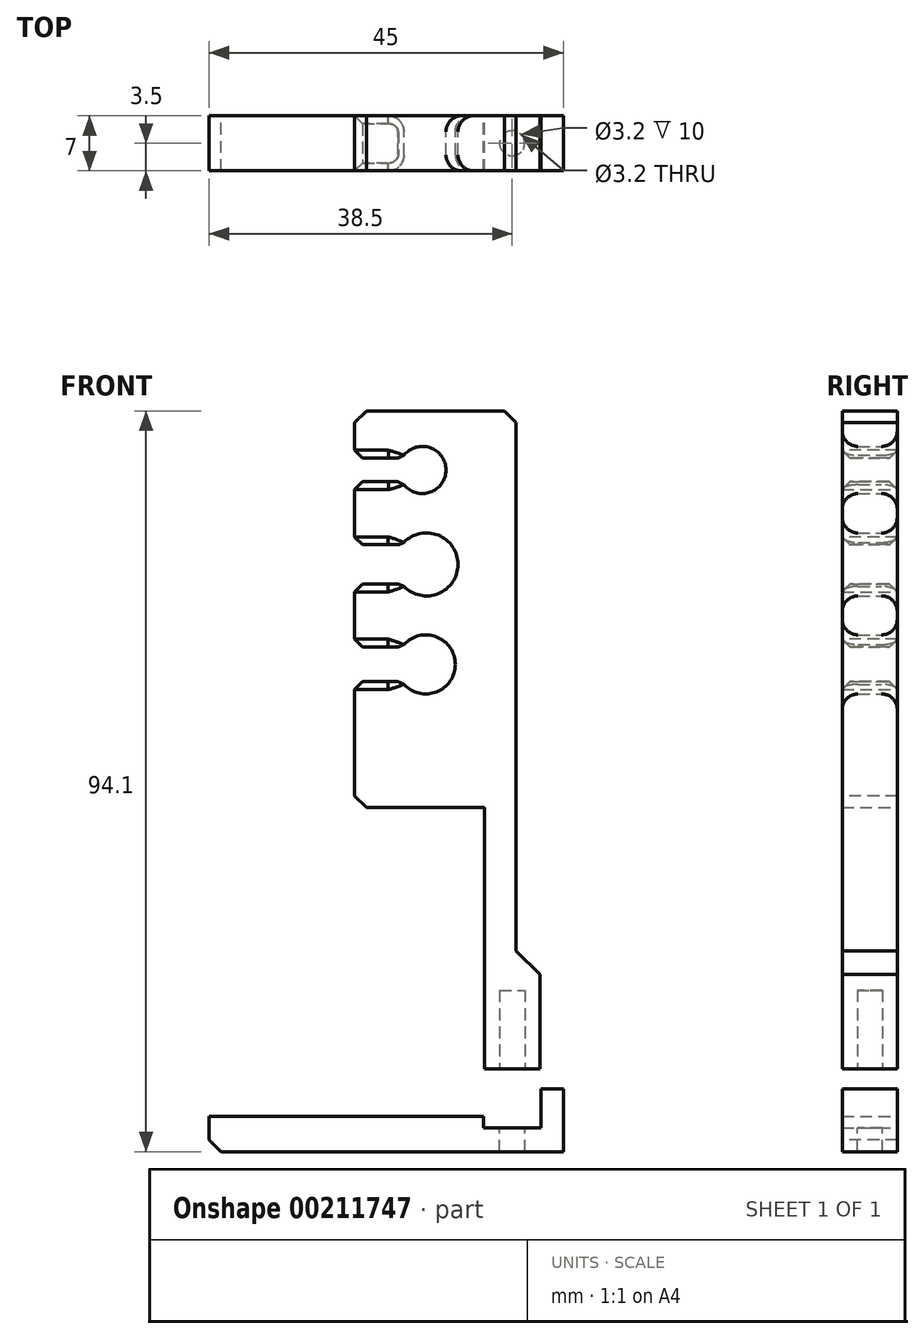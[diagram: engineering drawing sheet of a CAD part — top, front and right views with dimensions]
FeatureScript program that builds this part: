
annotation { "Feature Type Name" : "Feature", "Feature Type Description" : "" }
export const myFeature = defineFeature(function(context is Context, id is Id, definition is map)
    precondition{}
    {
        {
            var Q0;
            Q0=qCreatedBy(makeId("Front.planeOp"),FACE);
            var sketch = newSketch(context, id + "F0", { "sketchPlane" : qUnion([Q0])});
            skLineSegment(sketch, "E0", {"start": v(4, 50.4) * mm, "end": v(-16.51, 50.4) * mm});
            skLineSegment(sketch, "E1", {"start": v(-16.51, 50.4) * mm, "end": v(-16.51, 44.4) * mm});
            skLineSegment(sketch, "E2", {"start": v(-16.51, 44.4) * mm, "end": v(-10.51, 44.4) * mm});
            skLineSegment(sketch, "E3", {"start": v(-16.51, 41.4) * mm, "end": v(-10.51, 41.4) * mm});
            skArc(sketch, "E4", {"start": v(-10.51, 41.4) * mm, "mid": v(-4.91, 42.9) * mm, "end": v(-10.51, 44.4) * mm});
            skLineSegment(sketch, "E5", {"start": v(-16.51, 41.4) * mm, "end": v(-16.51, 33.4) * mm});
            skLineSegment(sketch, "E6", {"start": v(-16.51, 33.4) * mm, "end": v(-10.51, 33.4) * mm});
            skLineSegment(sketch, "E7", {"start": v(-10.5, 28.4) * mm, "end": v(-16.51, 28.4) * mm});
            skLineSegment(sketch, "E8", {"start": v(-16.51, 28.4) * mm, "end": v(-16.51, 20.4) * mm});
            skArc(sketch, "E9", {"start": v(-10.5, 28.4) * mm, "mid": v(-3.39, 30.9) * mm, "end": v(-10.51, 33.4) * mm});
            skLineSegment(sketch, "E10", {"start": v(-16.51, 20.4) * mm, "end": v(-10.51, 20.4) * mm});
            skLineSegment(sketch, "E11", {"start": v(-10.51, 16) * mm, "end": v(-16.51, 16) * mm});
            skArc(sketch, "E12", {"start": v(-10.51, 16) * mm, "mid": v(-3.72, 18.2) * mm, "end": v(-10.51, 20.4) * mm});
            skLineSegment(sketch, "E13.0", {"start": v(3.5, -43.7) * mm, "end": v(-35, -43.7) * mm});
            skPoint(sketch, "E14.end.orphan", {"position": v(-10.51, 18.2) * mm});
            skPoint(sketch, "E15.end.orphan", {"position": v(-10.51, 30.9) * mm});
            skPoint(sketch, "E16.orphan", {"position": v(-20, 0) * mm});
            skLineSegment(sketch, "E17", {"start": v(-35, -39.2) * mm, "end": v(-35, -43.7) * mm});
            skLineSegment(sketch, "E18.trimOffspring", {"start": v(-16.51, 16) * mm, "end": v(-16.51, 0) * mm});
            skPoint(sketch, "E19.start.orphan", {"position": v(0, 0) * mm});
            skLineSegment(sketch, "E20", {"start": v(0, -33.2) * mm, "end": v(0, 0) * mm});
            skLineSegment(sketch, "E21", {"start": v(4, 0.1) * mm, "end": v(4, -21.2) * mm});
            skLineSegment(sketch, "E22", {"start": v(-16.51, 0) * mm, "end": v(0, 0) * mm});
            skLineSegment(sketch, "E23", {"start": v(4, 50.4) * mm, "end": v(4, 0.1) * mm});
            skLineSegment(sketch, "E24", {"start": v(3.5, -43.7) * mm, "end": v(6.5, -43.7) * mm});
            skLineSegment(sketch, "E25", {"start": v(6.5, -43.7) * mm, "end": v(6.5, -40.7) * mm});
            skLineSegment(sketch, "E26", {"start": v(0, -33.2) * mm, "end": v(4, -33.2) * mm});
            skLineSegment(sketch, "E27", {"start": v(4, -33.2) * mm, "end": v(7, -33.2) * mm});
            skPoint(sketch, "E28.end.orphan", {"position": v(3.5, -40.7) * mm});
            skPoint(sketch, "E29.start.orphan", {"position": v(0, -40.7) * mm});
            skLineSegment(sketch, "E30", {"start": v(-35, -39.2) * mm, "end": v(-0.15, -39.2) * mm});
            skLineSegment(sketch, "E31", {"start": v(7, -33.2) * mm, "end": v(7, -21.2) * mm});
            skLineSegment(sketch, "E32", {"start": v(7, -21.2) * mm, "end": v(4, -21.2) * mm});
            skLineSegment(sketch, "E33", {"start": v(6.5, -43.7) * mm, "end": v(10, -43.7) * mm});
            skLineSegment(sketch, "E34", {"start": v(10, -43.7) * mm, "end": v(10, -35.7) * mm});
            skLineSegment(sketch, "E35", {"start": v(10, -35.7) * mm, "end": v(7.15, -35.7) * mm});
            skLineSegment(sketch, "E36", {"start": v(6.5, -40.7) * mm, "end": v(0, -40.7) * mm});
            skLineSegment(sketch, "E37", {"start": v(6.5, -40.7) * mm, "end": v(7.15, -40.7) * mm});
            skLineSegment(sketch, "E38", {"start": v(7.15, -40.7) * mm, "end": v(7.15, -35.7) * mm});
            skLineSegment(sketch, "E39", {"start": v(0, -40.7) * mm, "end": v(-0.15, -40.7) * mm});
            skLineSegment(sketch, "E40", {"start": v(-0.15, -40.7) * mm, "end": v(-0.15, -39.2) * mm});
            skPoint(sketch, "E41.orphan", {"position": v(6.5, -35.7) * mm});
            skPoint(sketch, "E42.orphan", {"position": v(6.5, -39.2) * mm});
            skSolve(sketch);
        }
        {
            var Q0;
            Q0 = qSketchRegion(id + "F0", true);
            extrude(context, id + "F1", {"entities" : qUnion([Q0]), "depth" : 7 * mm});
        }
        {
            var Q0;
            Q0=makeQuery(id+"F1.opExtrude","CAP_EDGE",EDGE,{"disambiguationData":[OSD([sQuery(id+"F0.wireOp",EDGE,"E12")])],"isStart":false});
            var Q1;
            Q1=makeQuery(id+"F1.opExtrude","CAP_EDGE",EDGE,{"disambiguationData":[OSD([sQuery(id+"F0.wireOp",EDGE,"E9")])],"isStart":false});
            var Q2;
            Q2=makeQuery(id+"F1.opExtrude","CAP_EDGE",EDGE,{"disambiguationData":[OSD([sQuery(id+"F0.wireOp",EDGE,"E4")])],"isStart":false});
            var Q3;
            Q3=makeQuery(id+"F1.opExtrude","CAP_EDGE",EDGE,{"disambiguationData":[OSD([sQuery(id+"F0.wireOp",EDGE,"E4")])],"isStart":true});
            var Q4;
            Q4=makeQuery(id+"F1.opExtrude","CAP_EDGE",EDGE,{"disambiguationData":[OSD([sQuery(id+"F0.wireOp",EDGE,"E9")])],"isStart":true});
            var Q5;
            Q5=makeQuery(id+"F1.opExtrude","CAP_EDGE",EDGE,{"disambiguationData":[OSD([sQuery(id+"F0.wireOp",EDGE,"E12")])],"isStart":true});
            fillet(context, id + "F2", {"entities" : qUnion([Q0, Q1, Q2, Q3, Q4, Q5]), "radius" : 2 * mm, "tangentPropagation" : true, "allowEdgeOverflow" : false});
        }
        {
            var Q0;
            Q0=makeQuery(id+"F1.opExtrude","SWEPT_EDGE",EDGE,{"disambiguationData":[OSD([sQuery(id+"F0.wireOp",EDGE,"E11"),sQuery(id+"F0.wireOp",EDGE,"E18.trimOffspring")])]});
            var Q1;
            Q1=makeQuery(id+"F1.opExtrude","SWEPT_EDGE",EDGE,{"disambiguationData":[OSD([sQuery(id+"F0.wireOp",EDGE,"E10"),sQuery(id+"F0.wireOp",EDGE,"E8")])]});
            var Q2;
            Q2=makeQuery(id+"F1.opExtrude","SWEPT_EDGE",EDGE,{"disambiguationData":[OSD([sQuery(id+"F0.wireOp",EDGE,"E7"),sQuery(id+"F0.wireOp",EDGE,"E8")])]});
            var Q3;
            Q3=makeQuery(id+"F1.opExtrude","SWEPT_EDGE",EDGE,{"disambiguationData":[OSD([sQuery(id+"F0.wireOp",EDGE,"E6"),sQuery(id+"F0.wireOp",EDGE,"E5")])]});
            var Q4;
            Q4=makeQuery(id+"F1.opExtrude","SWEPT_EDGE",EDGE,{"disambiguationData":[OSD([sQuery(id+"F0.wireOp",EDGE,"E3"),sQuery(id+"F0.wireOp",EDGE,"E5")])]});
            var Q5;
            Q5=makeQuery(id+"F1.opExtrude","SWEPT_EDGE",EDGE,{"disambiguationData":[OSD([sQuery(id+"F0.wireOp",EDGE,"E1"),sQuery(id+"F0.wireOp",EDGE,"E2")])]});
            var Q6;
            Q6=makeQuery(id+"F1.opExtrude","SWEPT_EDGE",EDGE,{"disambiguationData":[OSD([sQuery(id+"F0.wireOp",EDGE,"E11"),sQuery(id+"F0.wireOp",EDGE,"E12")])]});
            var Q7;
            Q7=makeQuery(id+"F1.opExtrude","SWEPT_EDGE",EDGE,{"disambiguationData":[OSD([sQuery(id+"F0.wireOp",EDGE,"E7"),sQuery(id+"F0.wireOp",EDGE,"E9")])]});
            var Q8;
            Q8=makeQuery(id+"F1.opExtrude","SWEPT_EDGE",EDGE,{"disambiguationData":[OSD([sQuery(id+"F0.wireOp",EDGE,"E3"),sQuery(id+"F0.wireOp",EDGE,"E4")])]});
            var Q9;
            Q9=makeQuery(id+"F1.opExtrude","SWEPT_EDGE",EDGE,{"disambiguationData":[OSD([sQuery(id+"F0.wireOp",EDGE,"E10"),sQuery(id+"F0.wireOp",EDGE,"E12")])]});
            var Q10;
            Q10=makeQuery(id+"F1.opExtrude","SWEPT_EDGE",EDGE,{"disambiguationData":[OSD([sQuery(id+"F0.wireOp",EDGE,"E6"),sQuery(id+"F0.wireOp",EDGE,"E9")])]});
            var Q11;
            Q11=makeQuery(id+"F1.opExtrude","SWEPT_EDGE",EDGE,{"disambiguationData":[OSD([sQuery(id+"F0.wireOp",EDGE,"E2"),sQuery(id+"F0.wireOp",EDGE,"E4")])]});
            chamfer(context, id + "F3", {"entities" : qUnion([Q0, Q1, Q2, Q3, Q4, Q5, Q6, Q7, Q8, Q9, Q10, Q11]), "width" : 1 * mm, "tangentPropagation" : true});
        }
        {
            var Q0;
            Q0=makeQuery(id+"F1.opExtrude","SWEPT_EDGE",EDGE,{"disambiguationData":[OSD([sQuery(id+"F0.wireOp",EDGE,"e3IPGrI8-xTFE-Wd2V-Q8Uj-KyzggoQHqLMG"),sQuery(id+"F0.wireOp",EDGE,"EqLzV6Df-d4xl-XVBd-FW3C-owhAdKDcz0o1")])]});
            var Q1;
            Q1=makeQuery(id+"F1.opExtrude","SWEPT_EDGE",EDGE,{"disambiguationData":[OSD([sQuery(id+"F0.wireOp",EDGE,"e3IPGrI8-xTFE-Wd2V-Q8Uj-KyzggoQHqLMG"),sQuery(id+"F0.wireOp",EDGE,"E18.trimOffspring")])]});
            var Q2;
            Q2=makeQuery(id+"F1.opExtrude","SWEPT_EDGE",EDGE,{"disambiguationData":[OSD([sQuery(id+"F0.wireOp",EDGE,"EqLzV6Df-d4xl-XVBd-FW3C-owhAdKDcz0o1"),sQuery(id+"F0.wireOp",EDGE,"OC7CJrtK-ZygH-mjQ6-sM5x-xopy489lml2c")])]});
            var Q3;
            Q3=makeQuery(id+"F1.opExtrude","SWEPT_EDGE",EDGE,{"disambiguationData":[OSD([sQuery(id+"F0.wireOp",EDGE,"ufyolKId-o4on-zhkq-HMRE-RqeXRvdZu1ue"),sQuery(id+"F0.wireOp",EDGE,"OC7CJrtK-ZygH-mjQ6-sM5x-xopy489lml2c")])]});
            var Q4;
            Q4=makeQuery(id+"F1.opExtrude","SWEPT_EDGE",EDGE,{"disambiguationData":[OSD([sQuery(id+"F0.wireOp",EDGE,"E19"),sQuery(id+"F0.wireOp",EDGE,"E29")])]});
            var Q5;
            Q5=makeQuery(id+"F1.opExtrude","SWEPT_EDGE",EDGE,{"disambiguationData":[OSD([sQuery(id+"F0.wireOp",EDGE,"E13.0"),sQuery(id+"F0.wireOp",EDGE,"E17")])]});
            var Q6;
            Q6=makeQuery(id+"F1.opExtrude","SWEPT_EDGE",EDGE,{"disambiguationData":[OSD([sQuery(id+"F0.wireOp",EDGE,"E0"),sQuery(id+"F0.wireOp",EDGE,"ufyolKId-o4on-zhkq-HMRE-RqeXRvdZu1ue")])]});
            chamfer(context, id + "F4", {"entities" : qUnion([Q0, Q1, Q2, Q3, Q4, Q5, Q6]), "width" : 1.5 * mm, "tangentPropagation" : true});
        }
        {
            var Q0;
            Q0=makeQuery(id+"F1.opExtrude","SWEPT_BODY",BODY,{"disambiguationData":[OSD([sQuery(id+"F0.wireOp",EDGE,"E0"),sQuery(id+"F0.wireOp",EDGE,"E29"),sQuery(id+"F0.wireOp",EDGE,"E1"),sQuery(id+"F0.wireOp",EDGE,"E2"),sQuery(id+"F0.wireOp",EDGE,"E3"),sQuery(id+"F0.wireOp",EDGE,"E4"),sQuery(id+"F0.wireOp",EDGE,"E6"),sQuery(id+"F0.wireOp",EDGE,"E7"),sQuery(id+"F0.wireOp",EDGE,"E9"),sQuery(id+"F0.wireOp",EDGE,"E10"),sQuery(id+"F0.wireOp",EDGE,"E11"),sQuery(id+"F0.wireOp",EDGE,"E12"),sQuery(id+"F0.wireOp",EDGE,"E13.0"),sQuery(id+"F0.wireOp",EDGE,"E17"),sQuery(id+"F0.wireOp",EDGE,"E18.trimOffspring"),sQuery(id+"F0.wireOp",EDGE,"E8"),sQuery(id+"F0.wireOp",EDGE,"E5"),sQuery(id+"F0.wireOp",EDGE,"E20"),sQuery(id+"F0.wireOp",EDGE,"E21"),sQuery(id+"F0.wireOp",EDGE,"E22"),sQuery(id+"F0.wireOp",EDGE,"E23"),sQuery(id+"F0.wireOp",EDGE,"iDiGlzHj-Hnh1-mIO6-iq0J-lUeF73iVNaqo"),sQuery(id+"F0.wireOp",EDGE,"E24"),sQuery(id+"F0.wireOp",EDGE,"E25")])]});
            transform(context, id + "F5", {"entities" : qUnion([Q0]), "transformType" : TransformType.TRANSLATION_3D, "dx" : 0 * mm, "dy" : 0 * mm, "dz" : 0 * mm, "makeCopy" : true});
        }
        {
            var Q0;
            Q0=makeQuery(id+"F5.opPattern","COPY",BODY,{"derivedFrom":makeQuery(id+"F1.opExtrude","SWEPT_BODY",BODY,{"disambiguationData":[OSD([sQuery(id+"F0.wireOp",EDGE,"E0"),sQuery(id+"F0.wireOp",EDGE,"E29"),sQuery(id+"F0.wireOp",EDGE,"E1"),sQuery(id+"F0.wireOp",EDGE,"E2"),sQuery(id+"F0.wireOp",EDGE,"E3"),sQuery(id+"F0.wireOp",EDGE,"E4"),sQuery(id+"F0.wireOp",EDGE,"E6"),sQuery(id+"F0.wireOp",EDGE,"E7"),sQuery(id+"F0.wireOp",EDGE,"E9"),sQuery(id+"F0.wireOp",EDGE,"E10"),sQuery(id+"F0.wireOp",EDGE,"E11"),sQuery(id+"F0.wireOp",EDGE,"E12"),sQuery(id+"F0.wireOp",EDGE,"E13.0"),sQuery(id+"F0.wireOp",EDGE,"E17"),sQuery(id+"F0.wireOp",EDGE,"E18.trimOffspring"),sQuery(id+"F0.wireOp",EDGE,"E8"),sQuery(id+"F0.wireOp",EDGE,"E5"),sQuery(id+"F0.wireOp",EDGE,"E20"),sQuery(id+"F0.wireOp",EDGE,"E21"),sQuery(id+"F0.wireOp",EDGE,"E22"),sQuery(id+"F0.wireOp",EDGE,"E23"),sQuery(id+"F0.wireOp",EDGE,"iDiGlzHj-Hnh1-mIO6-iq0J-lUeF73iVNaqo"),sQuery(id+"F0.wireOp",EDGE,"E24"),sQuery(id+"F0.wireOp",EDGE,"E25")])]}),"instanceName":"1"});
            deleteBodies(context, id + "F6", {"entities" : qUnion([Q0])});
        }
        {
            var Q0;
            Q0=makeQuery(id+"F1.opExtrude","SWEPT_FACE",FACE,{"disambiguationData":[OSD([sQuery(id+"F0.wireOp",EDGE,"E26"),sQuery(id+"F0.wireOp",EDGE,"E27")])]});
            var sketch = newSketch(context, id + "F7", { "sketchPlane" : qUnion([Q0])});
            skLineSegment(sketch, "E43", {"start": v(0, 7) * mm, "end": v(1.38, 5.62) * mm});
            skLineSegment(sketch, "E44", {"start": v(0, 0) * mm, "end": v(1.38, 1.38) * mm});
            skCircle(sketch, "E45", {"center": v(3.5, 3.5) * mm, "radius": 3 * mm});
            skLineSegment(sketch, "E46.trimOffspring", {"start": v(5.62, 1.38) * mm, "end": v(7, 0) * mm});
            skLineSegment(sketch, "E47.trimOffspring", {"start": v(5.62, 5.62) * mm, "end": v(7, 7) * mm});
            skCircle(sketch, "E48", {"center": v(3.5, 3.5) * mm, "radius": 1.6 * mm});
            skSolve(sketch);
        }
        {
            var Q0;
            Q0=makeQuery(id+"F7.imprint","IMPRINT",FACE,{"disambiguationData":[TD([[makeQuery(id+"F7.imprint","IMPRINT",EDGE,{"derivedFrom":sQuery(id+"F7.wireOp",EDGE,"E48")}),1.0]])]});
            extrude(context, id + "F8", {"entities" : qUnion([Q0]), "operationType" : NewBodyOperationType.REMOVE, "oppositeDirection" : true, "depth" : 10 * mm});
        }
        {
            var Q0;
            Q0=makeQuery(id+"F1.opExtrude","SWEPT_EDGE",EDGE,{"disambiguationData":[OSD([sQuery(id+"F0.wireOp",EDGE,"E21"),sQuery(id+"F0.wireOp",EDGE,"E32")])]});
            chamfer(context, id + "F9", {"entities" : qUnion([Q0]), "width" : 3 * mm, "tangentPropagation" : true});
        }
        {
            var Q0;
            Q0=makeQuery(id+"F1.opExtrude","SWEPT_FACE",FACE,{"disambiguationData":[OSD([sQuery(id+"F0.wireOp",EDGE,"E36"),sQuery(id+"F0.wireOp",EDGE,"E37"),sQuery(id+"F0.wireOp",EDGE,"E39")])]});
            var sketch = newSketch(context, id + "F10", { "sketchPlane" : qUnion([Q0])});
            skCircle(sketch, "E49", {"center": v(3.5, -3.5) * mm, "radius": 1.6 * mm});
            skPoint(sketch, "E50.orphan", {"position": v(-0.15, 0) * mm});
            skPoint(sketch, "E51.orphan", {"position": v(7.15, -7) * mm});
            skSolve(sketch);
        }
        {
            var Q0;
            Q0 = qSketchRegion(id + "F10", true);
            extrude(context, id + "F11", {"entities" : qUnion([Q0]), "operationType" : NewBodyOperationType.REMOVE, "oppositeDirection" : true, "depth" : 5 * mm});
        }
    });
